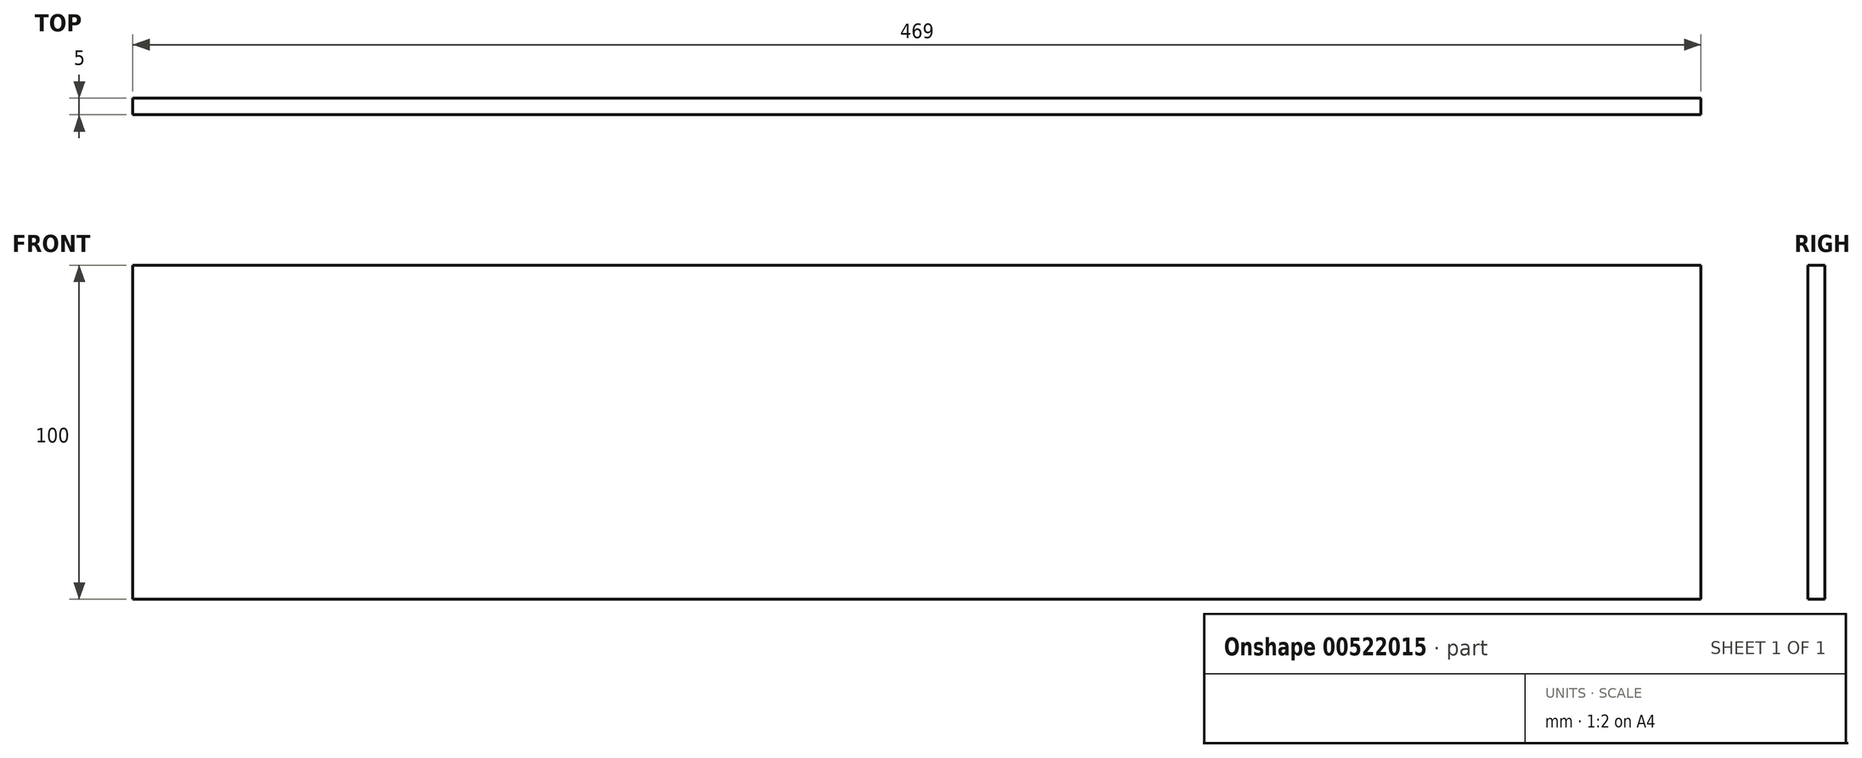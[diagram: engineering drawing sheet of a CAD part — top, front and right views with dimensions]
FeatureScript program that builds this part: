
annotation { "Feature Type Name" : "Feature", "Feature Type Description" : "" }
export const myFeature = defineFeature(function(context is Context, id is Id, definition is map)
    precondition{}
    {
        {
            var Q0;
            Q0=qCreatedBy(makeId("Front.planeOp"),FACE);
            var sketch = newSketch(context, id + "F0", { "sketchPlane" : qUnion([Q0])});
            skLineSegment(sketch, "E0.bottom", {"start": v(0, 0) * mm, "end": v(469, 0) * mm});
            skLineSegment(sketch, "E0.top", {"start": v(0, 100) * mm, "end": v(469, 100) * mm});
            skLineSegment(sketch, "E0.left", {"start": v(0, 0) * mm, "end": v(0, 100) * mm});
            skLineSegment(sketch, "E0.right", {"start": v(469, 0) * mm, "end": v(469, 100) * mm});
            skSolve(sketch);
        }
        {
            var Q0;
            Q0=makeQuery(id+"F0.imprint","IMPRINT",FACE,{"disambiguationData":[TD([[makeQuery(id+"F0.imprint","IMPRINT",EDGE,{"derivedFrom":sQuery(id+"F0.wireOp",EDGE,"E0.bottom")}),1.0]])]});
            extrude(context, id + "F1", {"entities" : qUnion([Q0]), "depth" : 5 * mm, "offsetDistance" : 25 * mm});
        }
    });
